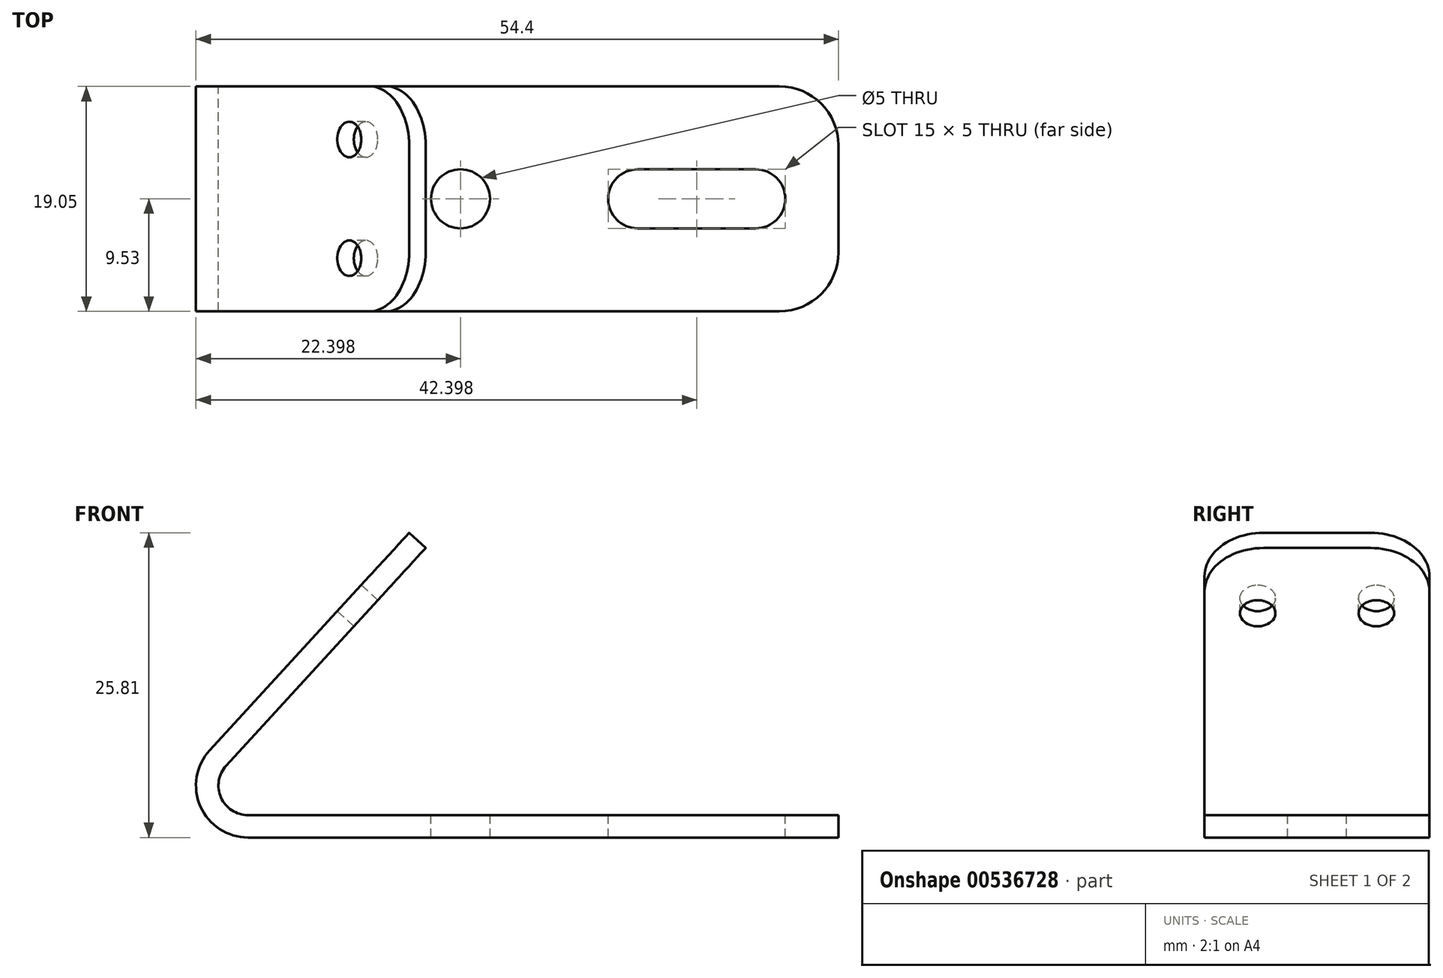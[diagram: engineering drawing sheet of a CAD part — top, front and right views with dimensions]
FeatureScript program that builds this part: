
annotation { "Feature Type Name" : "Feature", "Feature Type Description" : "" }
export const myFeature = defineFeature(function(context is Context, id is Id, definition is map)
    precondition{}
    {
        {
            var Q0;
            Q0=qCreatedBy(makeId("Front.planeOp"),FACE);
            var sketch = newSketch(context, id + "F0", { "sketchPlane" : qUnion([Q0])});
            skLineSegment(sketch, "E0", {"start": v(-15.14, 13.06) * mm, "end": v(34.86, 13.06) * mm});
            skLineSegment(sketch, "E1", {"start": v(34.86, 13.06) * mm, "end": v(34.86, 14.96) * mm});
            skLineSegment(sketch, "E2", {"start": v(34.86, 14.96) * mm, "end": v(-15.14, 14.96) * mm});
            skLineSegment(sketch, "E3", {"start": v(-15.14, 14.96) * mm, "end": v(-15.14, 13.06) * mm});
            skLineSegment(sketch, "E4", {"start": v(-16.99, 19.15) * mm, "end": v(-0.1, 37.58) * mm});
            skLineSegment(sketch, "E5", {"start": v(-0.1, 37.58) * mm, "end": v(-1.5, 38.87) * mm});
            skLineSegment(sketch, "E6", {"start": v(-1.5, 38.87) * mm, "end": v(-18.39, 20.43) * mm});
            skLineSegment(sketch, "E7", {"start": v(-18.39, 20.43) * mm, "end": v(-16.99, 19.15) * mm});
            skArc(sketch, "E8", {"start": v(-18.39, 20.43) * mm, "mid": v(-19.17, 15.69) * mm, "end": v(-15.14, 13.06) * mm});
            skArc(sketch, "E9", {"start": v(-16.99, 19.15) * mm, "mid": v(-17.43, 16.45) * mm, "end": v(-15.14, 14.96) * mm});
            skSolve(sketch);
        }
        {
            var Q0;
            Q0 = qSketchRegion(id + "F0", true);
            extrude(context, id + "F1", {"entities" : qUnion([Q0]), "depth" : 1.9 * mm, "offsetDistance" : 25 * mm});
        }
        {
            var Q0;
            Q0=makeQuery(id+"F1.opExtrude","CAP_FACE",FACE,{"disambiguationData":[OSD([sQuery(id+"F0.wireOp",EDGE,"E0"),sQuery(id+"F0.wireOp",EDGE,"E1"),sQuery(id+"F0.wireOp",EDGE,"E2"),sQuery(id+"F0.wireOp",EDGE,"E4"),sQuery(id+"F0.wireOp",EDGE,"E5"),sQuery(id+"F0.wireOp",EDGE,"E6"),sQuery(id+"F0.wireOp",EDGE,"E8"),sQuery(id+"F0.wireOp",EDGE,"E9")])],"isStart":false});
            extrude(context, id + "F2", {"entities" : qUnion([Q0]), "operationType" : NewBodyOperationType.ADD, "endBound" : BoundingType.SYMMETRIC, "depth" : 19.05 * mm, "offsetDistance" : 25 * mm});
        }
        {
            var Q0;
            {var subQ0=sQuery(id+"F0.wireOp",EDGE,"E2");Q0=makeQuery(id+"F2.boolean.opBoolean","MERGE",FACE,{"derivedFrom":[makeQuery(id+"F1.opExtrude","SWEPT_FACE",FACE,{"disambiguationData":[OSD([subQ0])]}),makeQuery(id+"F2.opExtrude","SWEPT_FACE",FACE,{"disambiguationData":[OSD([subQ0])]})]});}
            var sketch = newSketch(context, id + "F3", { "sketchPlane" : qUnion([Q0])});
            skLineSegment(sketch, "E10.0.0", {"start": v(34.86, -11.42) * mm, "end": v(34.86, 7.62) * mm});
            skLineSegment(sketch, "E10.0.1", {"start": v(34.86, 7.63) * mm, "end": v(-15.14, 7.63) * mm});
            skLineSegment(sketch, "E10.0.2", {"start": v(-15.14, 7.62) * mm, "end": v(-15.14, -11.42) * mm});
            skLineSegment(sketch, "E10.0.3", {"start": v(-15.14, -11.43) * mm, "end": v(34.86, -11.43) * mm});
            skCircle(sketch, "E11", {"center": v(2.86, -1.9) * mm, "radius": 2.5 * mm});
            skPoint(sketch, "E11.centerSnap0", {"position": v(-15.14, -1.9) * mm});
            skArc(sketch, "E12", {"start": v(17.86, 0.6) * mm, "mid": v(15.36, -1.9) * mm, "end": v(17.86, -4.4) * mm});
            skArc(sketch, "E13", {"start": v(27.86, -4.4) * mm, "mid": v(30.36, -1.9) * mm, "end": v(27.86, 0.6) * mm});
            skLineSegment(sketch, "E14", {"start": v(17.86, 0.6) * mm, "end": v(27.86, 0.6) * mm});
            skLineSegment(sketch, "E15", {"start": v(17.86, -4.4) * mm, "end": v(27.86, -4.4) * mm});
            skSolve(sketch);
        }
        {
            var Q0;
            Q0=makeQuery(id+"F3.imprint","IMPRINT",FACE,{"disambiguationData":[TD([[makeQuery(id+"F3.imprint","IMPRINT",EDGE,{"derivedFrom":sQuery(id+"F3.wireOp",EDGE,"E12")}),1.0]])]});
            var Q1;
            Q1=makeQuery(id+"F3.imprint","IMPRINT",FACE,{"disambiguationData":[TD([[makeQuery(id+"F3.imprint","IMPRINT",EDGE,{"derivedFrom":sQuery(id+"F3.wireOp",EDGE,"E11")}),1.0]])]});
            extrude(context, id + "F4", {"entities" : qUnion([Q0, Q1]), "operationType" : NewBodyOperationType.REMOVE, "endBound" : BoundingType.THROUGH_ALL, "oppositeDirection" : true, "depth" : 25 * mm, "offsetDistance" : 25 * mm});
        }
        {
            var Q0;
            {var subQ0=sQuery(id+"F0.wireOp",EDGE,"E6");Q0=makeQuery(id+"F2.boolean.opBoolean","MERGE",FACE,{"derivedFrom":[makeQuery(id+"F1.opExtrude","SWEPT_FACE",FACE,{"disambiguationData":[OSD([subQ0])]}),makeQuery(id+"F2.opExtrude","SWEPT_FACE",FACE,{"disambiguationData":[OSD([subQ0])]})]});}
            var sketch = newSketch(context, id + "F5", { "sketchPlane" : qUnion([Q0])});
            skCircle(sketch, "E16", {"center": v(6.93, 20.14) * mm, "radius": 1.5 * mm});
            skCircle(sketch, "E17", {"center": v(-3.12, 20.14) * mm, "radius": 1.5 * mm});
            skSolve(sketch);
        }
        {
            var Q0;
            Q0=makeQuery(id+"F5.imprint","IMPRINT",FACE,{"disambiguationData":[TD([[makeQuery(id+"F5.imprint","IMPRINT",EDGE,{"derivedFrom":sQuery(id+"F5.wireOp",EDGE,"E16")}),1.0]])]});
            var Q1;
            Q1=makeQuery(id+"F5.imprint","IMPRINT",FACE,{"disambiguationData":[TD([[makeQuery(id+"F5.imprint","IMPRINT",EDGE,{"derivedFrom":sQuery(id+"F5.wireOp",EDGE,"E17")}),1.0]])]});
            extrude(context, id + "F6", {"entities" : qUnion([Q0, Q1]), "operationType" : NewBodyOperationType.REMOVE, "oppositeDirection" : true, "depth" : 25 * mm, "offsetDistance" : 25 * mm});
        }
        {
            var Q0;
            Q0=makeQuery(id+"F2.opExtrude","CAP_EDGE",EDGE,{"disambiguationData":[OSD([sQuery(id+"F0.wireOp",EDGE,"E5")])],"isStart":false});
            var Q1;
            Q1=makeQuery(id+"F2.opExtrude","CAP_EDGE",EDGE,{"disambiguationData":[OSD([sQuery(id+"F0.wireOp",EDGE,"E5")])],"isStart":true});
            var Q2;
            Q2=makeQuery(id+"F2.opExtrude","CAP_EDGE",EDGE,{"disambiguationData":[OSD([sQuery(id+"F0.wireOp",EDGE,"E1")])],"isStart":true});
            var Q3;
            Q3=makeQuery(id+"F2.opExtrude","CAP_EDGE",EDGE,{"disambiguationData":[OSD([sQuery(id+"F0.wireOp",EDGE,"E1")])],"isStart":false});
            fillet(context, id + "F7", {"entities" : qUnion([Q0, Q1, Q2, Q3]), "radius" : 5 * mm, "tangentPropagation" : true, "allowEdgeOverflow" : false});
        }
    });
